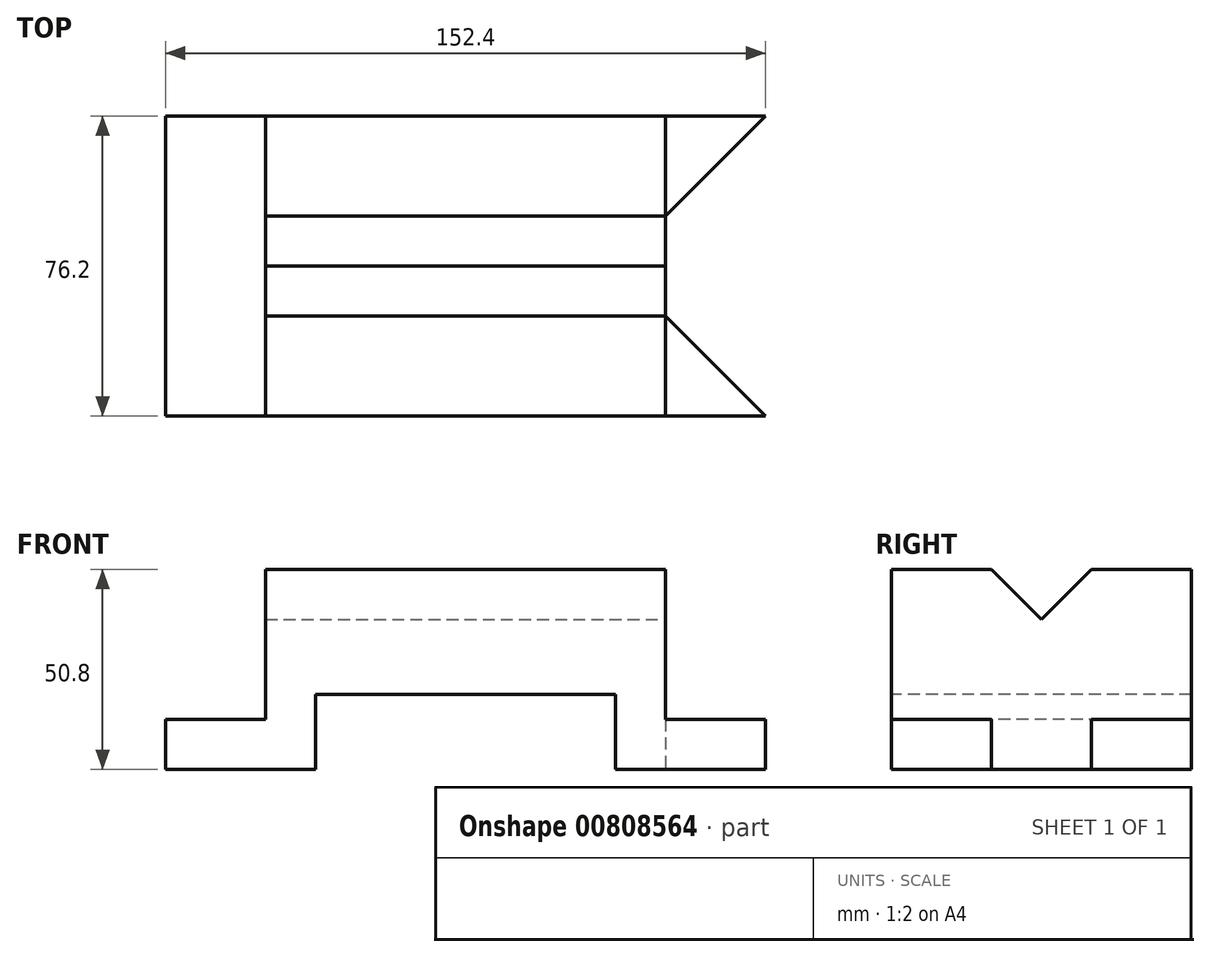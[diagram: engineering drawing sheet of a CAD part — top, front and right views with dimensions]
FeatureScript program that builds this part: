
annotation { "Feature Type Name" : "Feature", "Feature Type Description" : "" }
export const myFeature = defineFeature(function(context is Context, id is Id, definition is map)
    precondition{}
    {
        {
            var Q0;
            Q0=qCreatedBy(makeId("Top.planeOp"),FACE);
            var sketch = newSketch(context, id + "F0", { "sketchPlane" : qUnion([Q0])});
            skLineSegment(sketch, "E0.bottom", {"start": v(-54.43, 42.79) * mm, "end": v(-29.03, 42.79) * mm});
            skLineSegment(sketch, "E0.top", {"start": v(-54.43, -33.41) * mm, "end": v(-29.03, -33.41) * mm});
            skLineSegment(sketch, "E0.left", {"start": v(-54.43, 42.79) * mm, "end": v(-54.43, -33.41) * mm});
            skLineSegment(sketch, "E0.right", {"start": v(-29.03, 42.79) * mm, "end": v(-29.03, -33.41) * mm});
            skLineSegment(sketch, "E1.bottom", {"start": v(-29.03, 42.79) * mm, "end": v(72.57, 42.79) * mm});
            skLineSegment(sketch, "E1.top", {"start": v(-29.03, -33.41) * mm, "end": v(72.57, -33.41) * mm});
            skLineSegment(sketch, "E1.right", {"start": v(72.57, 42.79) * mm, "end": v(72.57, -33.41) * mm});
            skLineSegment(sketch, "E2", {"start": v(72.57, -33.41) * mm, "end": v(97.97, -33.41) * mm});
            skLineSegment(sketch, "E3", {"start": v(72.57, 42.79) * mm, "end": v(97.97, 42.79) * mm});
            skLineSegment(sketch, "E4", {"start": v(72.57, -8.01) * mm, "end": v(97.97, -33.41) * mm});
            skLineSegment(sketch, "E5", {"start": v(72.57, 17.39) * mm, "end": v(97.97, 42.79) * mm});
            skSolve(sketch);
        }
        {
            var Q0;
            {var subQ1=sQuery(id+"F0.wireOp",EDGE,"E1.bottom");Q0=makeQuery(id+"F0.imprint","IMPRINT",FACE,{"disambiguationData":[TD([[makeQuery(id+"F0.imprint","IMPRINT",EDGE,{"derivedFrom":subQ1}),-1.0]])]});}
            extrude(context, id + "F1", {"entities" : qUnion([Q0]), "depth" : 50.8 * mm, "offsetDistance" : 25.4 * mm});
        }
        {
            var Q0;
            Q0=makeQuery(id+"F0.imprint","IMPRINT",FACE,{"disambiguationData":[TD([[makeQuery(id+"F0.imprint","IMPRINT",EDGE,{"derivedFrom":sQuery(id+"F0.wireOp",EDGE,"E0.bottom")}),-1.0]])]});
            extrude(context, id + "F2", {"entities" : qUnion([Q0]), "operationType" : NewBodyOperationType.ADD, "depth" : 12.7 * mm, "offsetDistance" : 25.4 * mm});
        }
        {
            var Q0;
            {var subQ0=sQuery(id+"F0.wireOp",EDGE,"E3");Q0=makeQuery(id+"F0.imprint","IMPRINT",FACE,{"disambiguationData":[TD([[makeQuery(id+"F0.imprint","IMPRINT",EDGE,{"derivedFrom":subQ0}),-1.0]])]});}
            var Q1;
            {var subQ0=sQuery(id+"F0.wireOp",EDGE,"E2");Q1=makeQuery(id+"F0.imprint","IMPRINT",FACE,{"disambiguationData":[TD([[makeQuery(id+"F0.imprint","IMPRINT",EDGE,{"derivedFrom":subQ0}),1.0]])]});}
            extrude(context, id + "F3", {"entities" : qUnion([Q0, Q1]), "operationType" : NewBodyOperationType.ADD, "depth" : 12.7 * mm, "offsetDistance" : 25.4 * mm});
        }
        {
            var Q0;
            Q0=makeQuery(id+"F1.opExtrude","SWEPT_FACE",FACE,{"disambiguationData":[OSD([sQuery(id+"F0.wireOp",EDGE,"E1.right")])]});
            var sketch = newSketch(context, id + "F4", { "sketchPlane" : qUnion([Q0])});
            skLineSegment(sketch, "E6", {"start": v(4.69, 38.1) * mm, "end": v(17.39, 50.8) * mm});
            skLineSegment(sketch, "E7", {"start": v(-8.01, 50.8) * mm, "end": v(4.69, 38.1) * mm});
            skSolve(sketch);
        }
        {
            var Q0;
            {var subQ0=sQuery(id+"F4.wireOp",EDGE,"E6");Q0=makeQuery(id+"F4.imprint","IMPRINT",FACE,{"disambiguationData":[TD([[makeQuery(id+"F4.imprint","IMPRINT",EDGE,{"derivedFrom":subQ0}),1.0]])]});}
            extrude(context, id + "F5", {"entities" : qUnion([Q0]), "operationType" : NewBodyOperationType.ADD, "depth" : 25.4 * mm, "offsetDistance" : 25.4 * mm});
        }
        {
            var Q0;
            Q0=makeQuery(id+"F5.opExtrude","CAP_FACE",FACE,{"disambiguationData":[OSD([sQuery(id+"F0.wireOp",EDGE,"E1.right"),sQuery(id+"F4.wireOp",EDGE,"E6"),sQuery(id+"F4.wireOp",EDGE,"E7")])],"isStart":false});
            extrude(context, id + "F6", {"entities" : qUnion([Q0]), "operationType" : NewBodyOperationType.REMOVE, "oppositeDirection" : true, "depth" : 127 * mm, "offsetDistance" : 25.4 * mm});
        }
        {
            var Q0;
            Q0=makeQuery(id+"F3.boolean.opBoolean","MERGE",FACE,{"derivedFrom":[makeQuery(id+"F2.boolean.opBoolean","MERGE",FACE,{"derivedFrom":[makeQuery(id+"F1.opExtrude","SWEPT_FACE",FACE,{"disambiguationData":[OSD([sQuery(id+"F0.wireOp",EDGE,"E1.top")])]}),makeQuery(id+"F2.opExtrude","SWEPT_FACE",FACE,{"disambiguationData":[OSD([sQuery(id+"F0.wireOp",EDGE,"E0.top")])]})]}),makeQuery(id+"F3.opExtrude","SWEPT_FACE",FACE,{"disambiguationData":[OSD([sQuery(id+"F0.wireOp",EDGE,"E2")])]})]});
            var sketch = newSketch(context, id + "F7", { "sketchPlane" : qUnion([Q0])});
            skLineSegment(sketch, "E8", {"start": v(59.87, 0) * mm, "end": v(59.87, 19.05) * mm});
            skLineSegment(sketch, "E9", {"start": v(-16.33, 0) * mm, "end": v(-16.33, 19.05) * mm});
            skLineSegment(sketch, "E10", {"start": v(-16.33, 19.05) * mm, "end": v(59.87, 19.05) * mm});
            skPoint(sketch, "E11.start.orphan", {"position": v(-54.43, 0) * mm});
            skSolve(sketch);
        }
        {
            var Q0;
            {var subQ0=sQuery(id+"F7.wireOp",EDGE,"E8");Q0=makeQuery(id+"F7.imprint","IMPRINT",FACE,{"disambiguationData":[TD([[makeQuery(id+"F7.imprint","IMPRINT",EDGE,{"derivedFrom":subQ0}),1.0]])]});}
            extrude(context, id + "F8", {"entities" : qUnion([Q0]), "operationType" : NewBodyOperationType.REMOVE, "oppositeDirection" : true, "depth" : 101.6 * mm, "offsetDistance" : 25.4 * mm});
        }
    });
